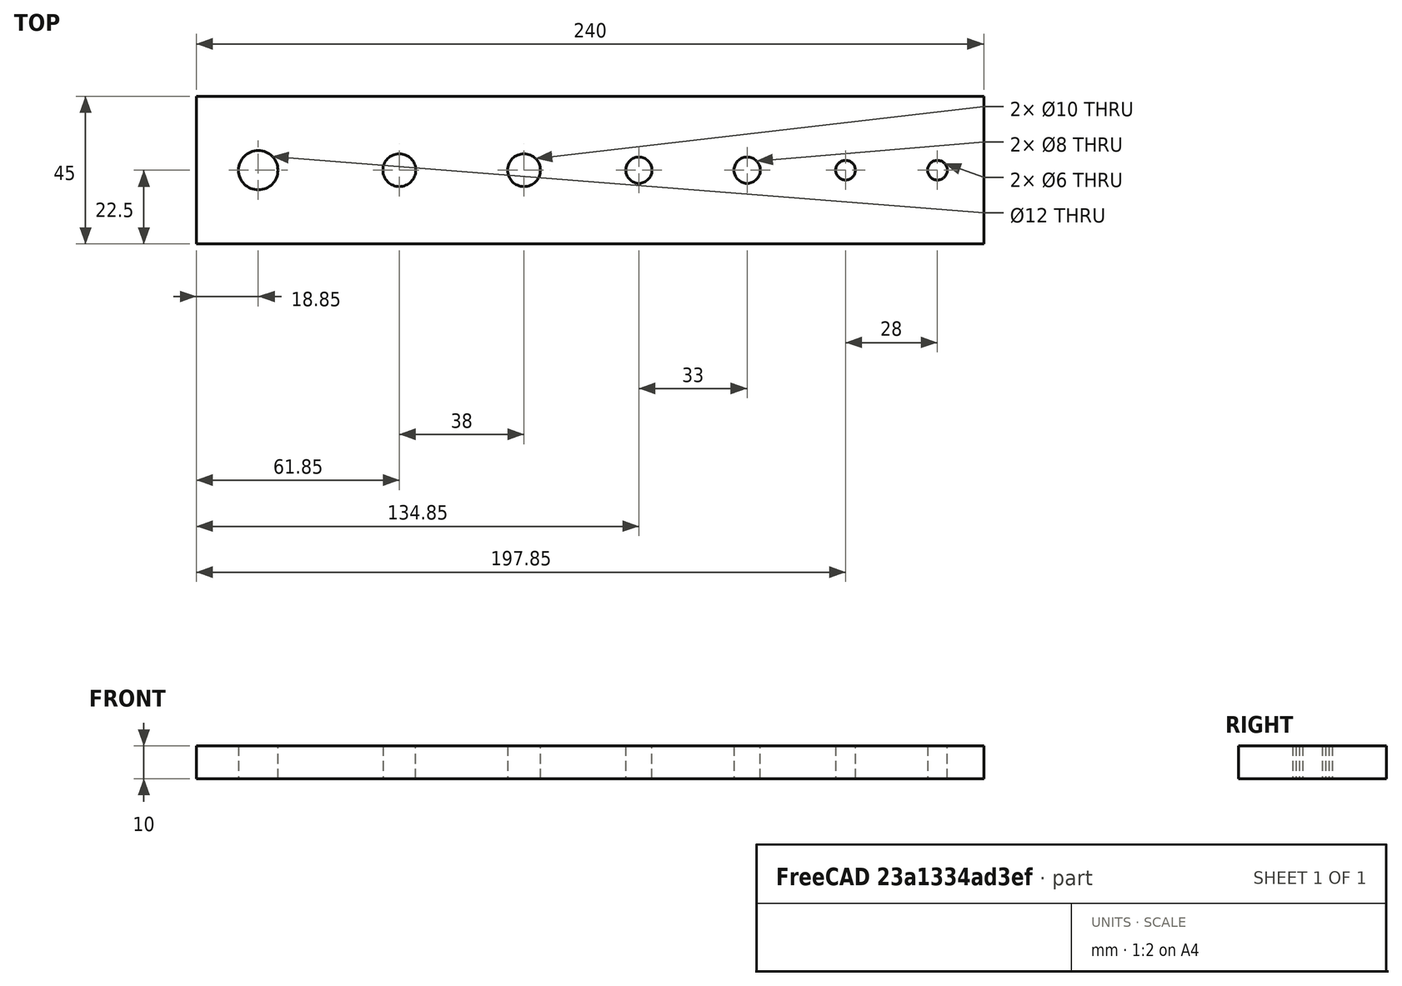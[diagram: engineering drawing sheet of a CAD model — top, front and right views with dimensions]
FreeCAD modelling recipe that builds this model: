
FCSTD DOCUMENT  (FreeCAD 2024.409R38991 (Git))
Label: SkadisScrewdrivers
License: All rights reserved
LicenseURL: https://en.wikipedia.org/wiki/All_rights_reserved
objects: Sketcher::SketchObject×1, PartDesign::Pad×1, PartDesign::Body×1
note: 6 computed .brp shape members not serialized (recipe doc carries the construction recipe); baked Part::Feature solids carry a one-line shape summary decoded from their .brp

FEATURE [Sketcher::SketchObject] Sketch
  ArcFitTolerance = 1e-06
  AttachmentSupport = -> [XY_Plane]
  ExternalBSplineMaxDegree = 5
  ExternalBSplineTolerance = 0.0001
  FullyConstrained = false
  InternalTolerance = 1e-06
  InvalidShape = false
  MakeInternals = false
  MapMode = 5
  Support = -> [XY_Plane]
  TreeRank = 11
  ValidateShape = false
  sketch-geometry (18):
    g0: LineSegment StartX=0 StartY=0 StartZ=0 EndX=240 EndY=0 EndZ=0
    g1: LineSegment StartX=240 StartY=0 StartZ=0 EndX=240 EndY=45 EndZ=0
    g2: LineSegment StartX=240 StartY=45 StartZ=0 EndX=0 EndY=45 EndZ=0
    g3: LineSegment StartX=0 StartY=45 StartZ=0 EndX=0 EndY=0 EndZ=0
    g4: LineSegment [constr] StartX=0 StartY=22.5 StartZ=0 EndX=240 EndY=22.5 EndZ=0
    g5: Circle CenterX=18.8504 CenterY=22.5 CenterZ=0 NormalX=0 NormalY=0 NormalZ=1 AngleXU=0 Radius=6
    g6: Circle CenterX=61.8504 CenterY=22.5 CenterZ=0 NormalX=0 NormalY=0 NormalZ=1 AngleXU=0 Radius=5
    g7: Circle [constr] CenterX=40.8504 CenterY=22.5 CenterZ=0 NormalX=0 NormalY=0 NormalZ=1 AngleXU=0 Radius=16
    g8: Circle [constr] CenterX=80.8504 CenterY=22.5 CenterZ=0 NormalX=0 NormalY=0 NormalZ=1 AngleXU=0 Radius=14
    g9: Circle CenterX=99.8504 CenterY=22.5 CenterZ=0 NormalX=0 NormalY=0 NormalZ=1 AngleXU=0 Radius=5
    g10: Circle [constr] CenterX=117.85 CenterY=22.5 CenterZ=0 NormalX=0 NormalY=0 NormalZ=1 AngleXU=0 Radius=13
    g11: Circle CenterX=134.85 CenterY=22.5 CenterZ=0 NormalX=0 NormalY=0 NormalZ=1 AngleXU=0 Radius=4
    g12: Circle [constr] CenterX=151.35 CenterY=22.5 CenterZ=0 NormalX=0 NormalY=0 NormalZ=1 AngleXU=0 Radius=12.5
    g13: Circle CenterX=167.85 CenterY=22.5 CenterZ=0 NormalX=0 NormalY=0 NormalZ=1 AngleXU=0 Radius=4
    g14: Circle [constr] CenterX=183.35 CenterY=22.5 CenterZ=0 NormalX=0 NormalY=0 NormalZ=1 AngleXU=0 Radius=11.5
    g15: Circle CenterX=197.85 CenterY=22.5 CenterZ=0 NormalX=0 NormalY=0 NormalZ=1 AngleXU=0 Radius=3
    g16: Circle [constr] CenterX=211.85 CenterY=22.5 CenterZ=0 NormalX=0 NormalY=0 NormalZ=1 AngleXU=0 Radius=11
    g17: Circle CenterX=225.85 CenterY=22.5 CenterZ=0 NormalX=0 NormalY=0 NormalZ=1 AngleXU=0 Radius=3
  constraints (53):
    c: Coincident(g0,g1)
    c: Coincident(g1,g2)
    c: Coincident(g2,g3)
    c: Coincident(g3,g0)
    c: Horizontal(g0)
    c: Horizontal(g2)
    c: Vertical(g1)
    c: Vertical(g3)
    c: Coincident(g0,g-1)
    c: DistanceX(g0,g0) = 240
    c: DistanceY(g3,g3) = 45
    c: PointOnObject(g4,g3)
    c: PointOnObject(g4,g1)
    c: Horizontal(g4)
    c: DistanceY(g0,g4) = 22.5
    c: PointOnObject(g5,g4)
    c: Diameter(g5) = 12
    c: PointOnObject(g6,g4)
    c: Diameter(g6) = 10
    c: Diameter(g7) = 32
    c: Tangent(g5,g7)
    c: Tangent(g7,g6)
    c: PointOnObject(g8,g4)
    c: Tangent(g6,g8)
    c: PointOnObject(g9,g4)
    c: Diameter(g9) = 10
    c: Tangent(g9,g8)
    c: PointOnObject(g10,g4)
    c: Tangent(g9,g10)
    c: PointOnObject(g11,g4)
    c: Diameter(g11) = 8
    c: PointOnObject(g7,g4)
    c: Tangent(g11,g10)
    c: PointOnObject(g12,g4)
    c: Tangent(g12,g11)
    c: PointOnObject(g13,g4)
    c: Tangent(g13,g12)
    c: PointOnObject(g14,g4)
    c: Diameter(g8) = 28
    c: Diameter(g10) = 26
    c: Diameter(g12) = 25
    c: Diameter(g14) = 23
    c: Tangent(g14,g13)
    c: Diameter(g13) = 8
    c: PointOnObject(g15,g4)
    c: Diameter(g15) = 6
    c: Tangent(g15,g14)
    c: PointOnObject(g16,g4)
    c: Diameter(g16) = 22
    c: Tangent(g16,g15)
    c: PointOnObject(g17,g4)
    c: Diameter(g17) = 6
    c: Tangent(g17,g16)
FEATURE [PartDesign::Pad] Pad
  AddSubType = 0
  AlongSketchNormal = false
  AutoTaperInnerAngle = true
  CheckUpToFaceLimits = true
  ClaimChildren = false
  Direction = (0,0,1)
  Fit = 0
  FitJoin = 0
  InnerFit = 0
  InnerFitJoin = 0
  InvalidShape = false
  Length = 10
  Length2 = 10
  Linearize = true
  NewSolid = false
  Profile = -> Sketch
  ReferenceAxis = -> Sketch [N_Axis]
  Suppress = false
  TaperInnerAngle = 0
  TaperInnerAngleRev = 0
  TreeRank = 12
  Type = 0
  ValidateShape = true
  _ProfileBasedVersion = 1
FEATURE [PartDesign::Body] Body
  AutoGroupSolids = false
  ClaimAllChildren = false
  ExportMode = 0
  Group = -> [Sketch,Pad]
  InvalidShape = false
  Origin = -> Origin
  Tip = -> Pad
  TreeRank = 10
  ValidateShape = false
  _ExportChildren = -> [Pad]
  _GroupVersion = 1
